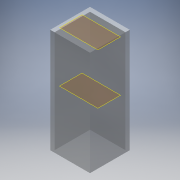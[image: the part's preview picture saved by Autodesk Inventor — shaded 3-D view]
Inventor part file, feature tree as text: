
AUTODESK INVENTOR PART (.ipt)
format: ipt  version: 2019 (Build 230136000, 136)  size: 116,224 bytes
history: native  units: in
note: dims shown in document units (in); Inventor stores cm internally (conversion verified against a paired STEP export)
features: plane x2, extrude x2, sketch x2
ambient origin geometry x8: Origin, YZ Plane, XZ Plane, XY Plane, X Axis, Y Axis, Z Axis, Center Point
bodies: Solid1 (feature_tree)
feature tree (6):
  plane  "Work Plane1"
  plane  "Work Plane2"
  extrude  "Extrusion1"  Depth=3.3in
  extrude  "Extrusion2"  Depth=0.2in
  sketch  "Sketch2"  dims[d0=4.7in d1=3.3in]
  sketch  "Sketch3"  dims[d2=3.3in d3=1.4in d4=0.4935in d5=0.2in d6=0.2in d7=0.2in d8=0.2in d9=10.0in d10=0.0in d11=0.2in d12=0.0in]
